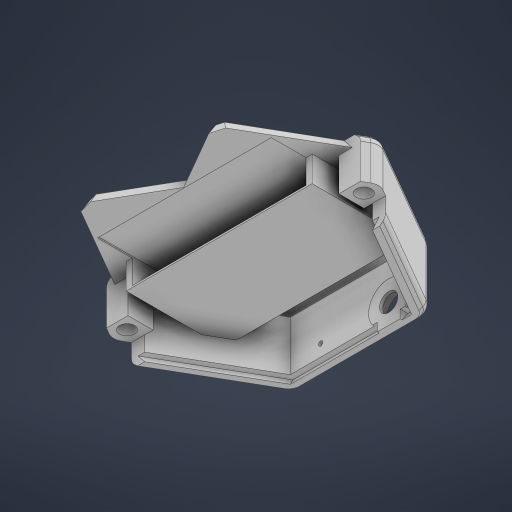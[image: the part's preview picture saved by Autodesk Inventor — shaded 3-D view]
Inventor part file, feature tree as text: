
AUTODESK INVENTOR PART (.ipt)
format: ipt  version: 2023 (Build 270158000, 158)  size: 951,296 bytes
history: native  units: in
note: dims shown in document units (in); Inventor stores cm internally (conversion verified against a paired STEP export)
features: extrude x27, sketch x17, move_body x15, direct_edit x10, draft x6, plane x3, fillet x3, chamfer x3, other x1
ambient origin geometry x8: Origin, YZ Plane, XZ Plane, XY Plane, X Axis, Y Axis, Z Axis, Center Point
bodies: Solid1 (feature_tree)
feature tree (85):
  sketch  "Sketch1"  dims[d0=1.939in d1=0.5118in d2=0.374in d3=0.4449in d4=0.0295in d5=0.0728in d6=0.1378in d7=0.0787in d8=0.0in d9=0.6181in d10=0.0in]
  extrude  "Extrusion1"  Depth=0.0787in TaperAngle=0.0deg
  extrude  "Extrusion2"  Depth=0.0906in
  extrude  "Extrusion3"  Depth=0.2205in TaperAngle=0.0deg
  sketch  "Sketch4"  dims[d15=0.0in d16=0.0in d17=0.2205in d18=0.0in]
  extrude  "Extrusion4"  Depth=1.5748in
  extrude  "Extrusion5"  Depth=0.0394in
  extrude  "Extrusion6"  Depth=0.2283in TaperAngle=0.0deg
  extrude  "Extrusion7"  Depth=0.0787in TaperAngle=0.0deg
  extrude  "Extrusion8"  Depth=0.3937in
  plane  "Work Plane1"
  extrude  "Extrusion9"  Depth=0.3937in TaperAngle=0.0deg
  extrude  "Extrusion10"  Depth=0.3937in TaperAngle=0.0deg
  plane  "Work Plane2"
  sketch  "Sketch7"  dims[d19=0.4764in d20=0.0in d21=1.5748in]
  extrude  "Extrusion11"  Depth=0.0787in TaperAngle=0.0deg
  extrude  "Extrusion12"  Depth=0.0787in
  extrude  "Extrusion14"  Depth=0.2405in
  extrude  "Extrusion15"  Depth=0.3937in TaperAngle=0.0deg
  direct_edit  "Direct Edit5"
  plane  "Work Plane3"
  sketch  "Sketch11"  dims[d32=0.0787in d33=0.0591in d34=0.0in]
  extrude  "Extrusion16"  Depth=0.3937in
  extrude  "Extrusion17"  [1 undecoded]
  draft  "FaceDraft1"
  draft  "FaceDraft2"
  draft  "FaceDraft3"
  extrude  "Extrusion18"  Depth=0.0787in TaperAngle=0.0deg
  draft  "FaceDraft5"
  direct_edit  "Direct Edit6"
  sketch  "Sketch12"  dims[d35=0.3937in d36=0.0in d38=0.2405in]
  sketch  "Sketch13"  dims[d40=0.0787in d41=0.3937in d42=0.0in]
  fillet  "Fillet1"  [1 undecoded]
  fillet  "Fillet2"  Radius=0.2405in
  chamfer  "Chamfer2"  Angle=90.0deg  [1 undecoded]
  fillet  "Fillet3"  Radius=0.2405in
  extrude  "Extrusion19"  Depth=0.0787in TaperAngle=0.0deg
  extrude  "Extrusion20"  Depth=0.0787in
  sketch  "Sketch15"  dims[d61=0.0689in d62=0.0in d72=0.0in d73=0.0in d74=0.0787in]
  sketch  "Sketch16"  dims[d75=0.0in d76=0.0in d77=0.0787in d81=0.0591in]
  extrude  "Extrusion22"  Depth=0.0787in
  extrude  "Extrusion23"  Depth=0.0787in
  direct_edit  "Direct Edit7"
  extrude  "Extrusion24"  Depth=0.0787in TaperAngle=45.0deg
  extrude  "Extrusion25"  Depth=0.0787in
  extrude  "Extrusion26"  Depth=0.0787in TaperAngle=0.0deg
  chamfer  "Chamfer3"  Distance=0.2008in
  extrude  "Extrusion27"  Depth=0.0787in
  draft  "FaceDraft6"
  draft  "FaceDraft7"
  direct_edit  "Direct Edit9"
  direct_edit  "Direct Edit10"
  extrude  "Extrusion28"  Depth=0.0787in
  direct_edit  "Direct Edit11"
  direct_edit  "Direct Edit12"
  direct_edit  "Direct Edit13"
  extrude  "Extrusion29"  TaperAngle=0.0deg  [1 undecoded]
  chamfer  "Chamfer4"  Distance=0.2953in
  direct_edit  "Direct Edit14"
  direct_edit  "Direct Edit15"
  sketch  "Sketch3"  dims[d11=0.5906in d12=0.0in d14=0.0906in]
  sketch  "Sketch9"  dims[d22=1.1811in d23=0.0394in]
  sketch  "Sketch10"  dims[d24=0.2441in d25=0.0in d26=0.2283in d27=0.0in]
  other  "Image1"
  sketch  "Sketch14"  dims[d43=0.3937in d44=0.0in d59=0.0689in d60=0.0in]
  sketch  "Sketch17"  dims[d82=90.0deg d83=0.2405in]
  sketch  "Sketch18"  dims[d84=0.0787in d85=0.3937in d86=0.0in]
  sketch  "Sketch19"  dims[d87=0.3937in d88=0.0in d89=0.2405in]
  sketch  "Sketch20"  dims[d90=-0.2061in d91=-0.2061in]
  sketch  "Sketch21"  dims[d93=0.5118in d94=0.0118in d95=0.0in d96=90.0deg d97=0.2405in d98=90.0deg d99=0.2405in d100=0.0in d101=0.0in d102=0.0157in d111=0.1969in d113=2.4409in d115=1.939in d116=0.5118in d117=0.374in d118=0.4134in d119=0.0295in d120=0.0728in d121=0.1378in d122=0.1181in d124=0.1575in d125=0.0492in d126=0.0787in d127=45.0deg d128=0.0787in d186=0.0236in d187=0.0in d188=0.2008in d189=0.1102in d190=0.1732in d191=0.0in d192=0.0in d193=0.2953in d196=0.7744in d197=0.1024in d198=0.0394in d199=0.0in d200=0.0in d201=0.2165in d202=0.3937in d203=0.0in d204=0.0in d205=0.0in d206=-0.4375in d207=0.1181in d208=0.0in d222=0.6871in d223=0.0in d224=0.0in d225=0.0118in d226=0.0in d227=0.0394in d228=0.0118in d229=45.0deg d234=45.0deg d235=0.3937in d236=0.0in d237=-0.2061in d238=-0.2061in d239=0.0in d240=0.0in d241=0.0091in d242=0.0in d243=0.0in d244=0.0091in d245=0.0in d246=0.0in d247=-0.0118in d248=0.0in d249=0.0in d250=-0.0118in d255=0.0394in d256=0.0in d257=0.0in d258=0.0in d259=-0.0098in d264=0.0in d265=0.0in d266=0.0591in d267=0.0in d268=0.0in d269=0.0591in d270=0.1496in d271=0.1417in d273=0.0in d274=0.0in d275=-0.0197in d276=0.0in d277=0.0in d278=0.0197in d280=0.1417in d281=0.1535in d282=0.0079in d283=0.0079in d286=0.1181in d287=0.4331in d288=0.1181in d289=0.0591in d290=0.0in d291=0.0591in d292=0.0787in d293=45.0deg d294=0.0073in d296=0.0in d297=0.0in d298=-0.0118in d299=0.0in d300=0.0in d301=0.0118in d45=0.0197in d46=0.0344in d47=0.0197in d48=0.0344in d103=0.0344in]
  move_body  "Move8"
  move_body  "Move9"
  move_body  "Move10"
  move_body  "Move11"
  move_body  "Move16"
  move_body  "Move17"
  move_body  "Move18"
  move_body  "Move19"
  move_body  "Move20"
  move_body  "Move21"
  move_body  "Move22"
  move_body  "Move23"
  move_body  "Move24"
  move_body  "Move25"
  move_body  "Move26"
note: 4 required parameter values undecoded (feature->parameter linkage not recoverable at this tier; creation-order binding heuristic only, values carry confidence <= 0.55)
